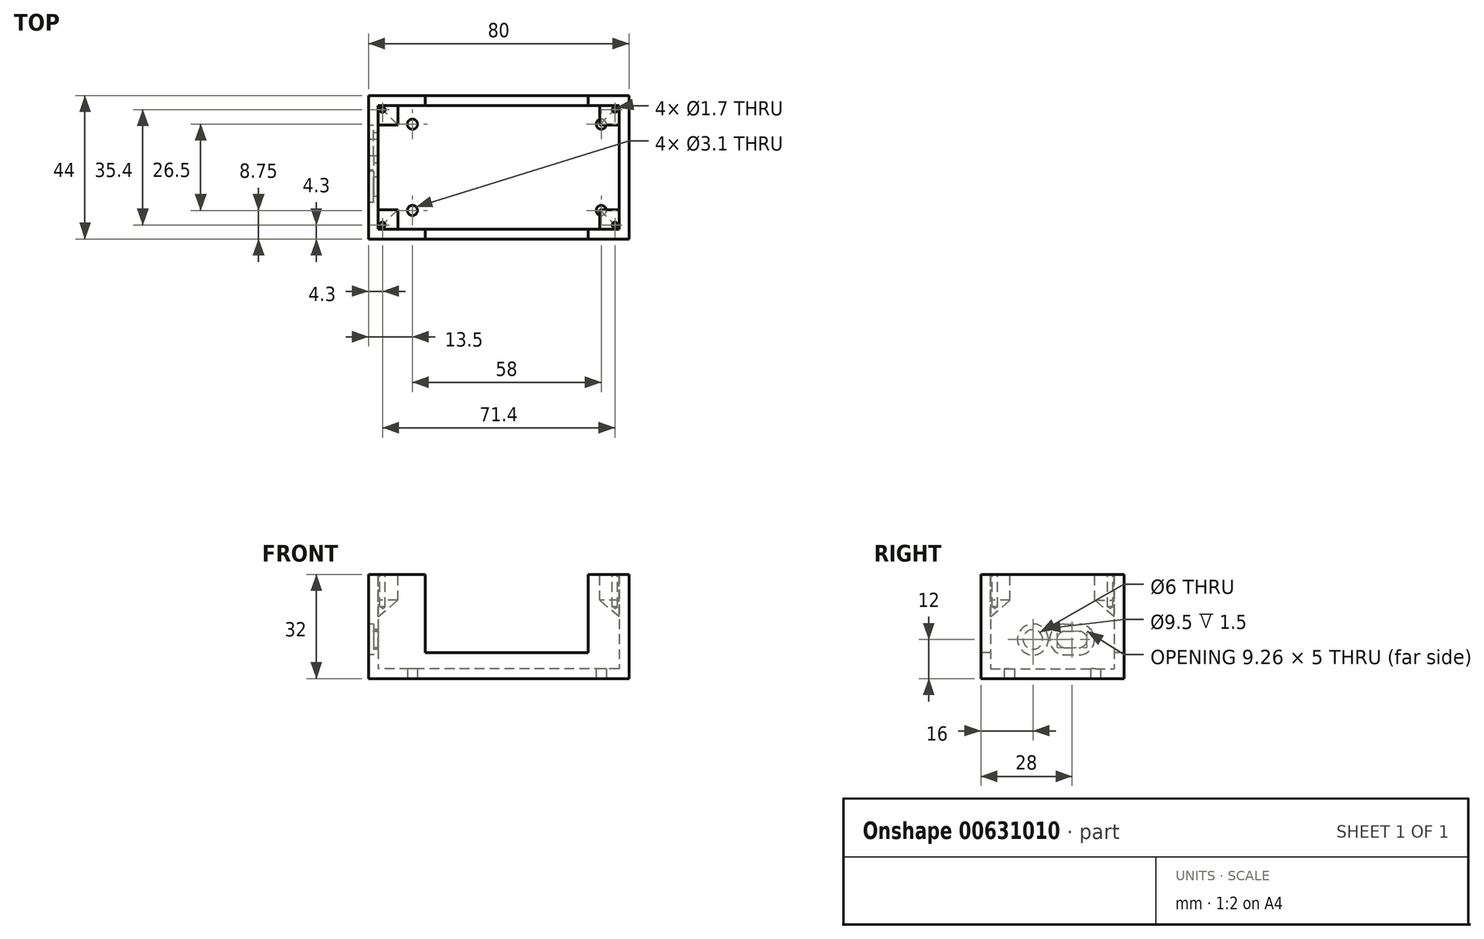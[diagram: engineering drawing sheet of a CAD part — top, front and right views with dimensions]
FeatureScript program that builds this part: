
annotation { "Feature Type Name" : "Feature", "Feature Type Description" : "" }
export const myFeature = defineFeature(function(context is Context, id is Id, definition is map)
    precondition{}
    {
        {
            var Q0;
            Q0=qCreatedBy(makeId("Top.planeOp"),FACE);
            var sketch = newSketch(context, id + "F0", { "sketchPlane" : qUnion([Q0])});
            skLineSegment(sketch, "E0.bottom", {"start": v(40, -22) * mm, "end": v(-40, -22) * mm});
            skLineSegment(sketch, "E0.top", {"start": v(40, 22) * mm, "end": v(-40, 22) * mm});
            skLineSegment(sketch, "E0.left", {"start": v(40, -22) * mm, "end": v(40, 22) * mm});
            skLineSegment(sketch, "E0.right", {"start": v(-40, -22) * mm, "end": v(-40, 22) * mm});
            skPoint(sketch, "E0.middle", {"position": v(0, 0) * mm});
            skSolve(sketch);
        }
        {
            var Q0;
            Q0=makeQuery(id+"F0.imprint","IMPRINT",FACE,{"disambiguationData":[TD([[makeQuery(id+"F0.imprint","IMPRINT",EDGE,{"derivedFrom":sQuery(id+"F0.wireOp",EDGE,"E0.bottom")}),-1.0]])]});
            extrude(context, id + "F1", {"entities" : qUnion([Q0]), "depth" : 32 * mm, "offsetDistance" : 25 * mm});
        }
        {
            var Q0;
            Q0=makeQuery(id+"F1.opExtrude","CAP_FACE",FACE,{"disambiguationData":[OSD([sQuery(id+"F0.wireOp",EDGE,"E0.bottom"),sQuery(id+"F0.wireOp",EDGE,"E0.top"),sQuery(id+"F0.wireOp",EDGE,"E0.left"),sQuery(id+"F0.wireOp",EDGE,"E0.right")])],"isStart":false});
            shell(context, id + "F2", {"entities" : qUnion([Q0]), "thickness" : 3 * mm});
        }
        {
            var Q0;
            Q0=makeQuery(id+"F1.opExtrude","SWEPT_FACE",FACE,{"disambiguationData":[OSD([sQuery(id+"F0.wireOp",EDGE,"E0.right")])]});
            var sketch = newSketch(context, id + "F3", { "sketchPlane" : qUnion([Q0])});
            skPoint(sketch, "E1", {"position": v(6, 12) * mm});
            skSolve(sketch);
        }
        {
            var Q0;
            {var subQ0=sQuery(id+"F0.wireOp",EDGE,"E0.right");Q0=makeQuery(id+"F3.imprint","IMPRINT",FACE,{"disambiguationData":[TD([[makeQuery(id+"F3.imprint","IMPRINT",EDGE,{"derivedFrom":makeQuery(id+"F1.opExtrude","CAP_EDGE",EDGE,{"disambiguationData":[OSD([subQ0])],"isStart":true})}),-1.0]])]});}
            var sketch = newSketch(context, id + "F4", { "sketchPlane" : qUnion([Q0])});
            skPoint(sketch, "E2", {"position": v(-6, 12) * mm});
            skPoint(sketch, "E3", {"position": v(-8.13, 12) * mm});
            skPoint(sketch, "E4", {"position": v(-3.87, 12) * mm});
            skSolve(sketch);
        }
        {
            var Q0;
            Q0=sQuery(id+"F3.wireOp",VERTEX,"E1");
            var Q1;
            Q1=makeQuery(id+"F1.opExtrude","SWEPT_BODY",BODY,{"disambiguationData":[OSD([sQuery(id+"F0.wireOp",EDGE,"E0.bottom"),sQuery(id+"F0.wireOp",EDGE,"E0.top"),sQuery(id+"F0.wireOp",EDGE,"E0.left"),sQuery(id+"F0.wireOp",EDGE,"E0.right")])]});
            hole(context, id + "F5", {"style" : HoleStyle.C_BORE, "endStyle" : HoleEndStyle.BLIND, "holeDiameter" : 6 * mm, "cBoreDiameter" : 9.5 * mm, "cBoreDepth" : 1.5 * mm, "majorDiameter" : 5 * mm, "holeDepth" : 10 * mm, "isTappedThrough" : true, "tappedDepth" : 12 * mm, "tapClearance" : 3, "locations" : qUnion([Q0]), "scope" : qUnion([Q1])});
        }
        {
            var Q0;
            Q0=sQuery(id+"F4.wireOp",VERTEX,"E3");
            var Q1;
            Q1=sQuery(id+"F4.wireOp",VERTEX,"E4");
            var Q2;
            Q2=makeQuery(id+"F1.opExtrude","SWEPT_BODY",BODY,{"disambiguationData":[OSD([sQuery(id+"F0.wireOp",EDGE,"E0.bottom"),sQuery(id+"F0.wireOp",EDGE,"E0.top"),sQuery(id+"F0.wireOp",EDGE,"E0.left"),sQuery(id+"F0.wireOp",EDGE,"E0.right")])]});
            hole(context, id + "F6", {"style" : HoleStyle.C_BORE, "endStyle" : HoleEndStyle.BLIND, "holeDiameter" : 5 * mm, "cBoreDiameter" : 9.5 * mm, "cBoreDepth" : 1.5 * mm, "majorDiameter" : 5 * mm, "holeDepth" : 10 * mm, "isTappedThrough" : true, "tappedDepth" : 12 * mm, "tapClearance" : 3, "locations" : qUnion([Q0, Q1]), "scope" : qUnion([Q2])});
        }
        {
            var Q0;
            Q0=makeQuery(id+"F1.opExtrude","SWEPT_FACE",FACE,{"disambiguationData":[OSD([sQuery(id+"F0.wireOp",EDGE,"E0.right")])]});
            var sketch = newSketch(context, id + "F7", { "sketchPlane" : qUnion([Q0])});
            skLineSegment(sketch, "E5.bottom", {"start": v(-3.5, 9.5) * mm, "end": v(-8.5, 9.5) * mm});
            skLineSegment(sketch, "E5.top", {"start": v(-3.5, 14.5) * mm, "end": v(-8.5, 14.5) * mm});
            skLineSegment(sketch, "E5.left", {"start": v(-3.5, 9.5) * mm, "end": v(-3.5, 14.5) * mm});
            skLineSegment(sketch, "E5.right", {"start": v(-8.5, 9.5) * mm, "end": v(-8.5, 14.5) * mm});
            skPoint(sketch, "E5.middle", {"position": v(-6, 12) * mm});
            skSolve(sketch);
        }
        {
            var Q0;
            {var subQ0=sQuery(id+"F7.wireOp",EDGE,"E5.top");var subQ1=makeQuery(id+"F6.hole-1.boolean.opBoolean","COPY",EDGE,{"derivedFrom":makeQuery(id+"F6.hole-1.opRevolve","SWEPT_EDGE",EDGE,{"disambiguationData":[OSD([sQuery(id+"F6.hole-1.sketch.wireOp",EDGE,"core_line_2"),sQuery(id+"F6.hole-1.sketch.wireOp",EDGE,"core_line_3")])]})});var subQ2=makeQuery(id+"F7.imprint","INTERSECT",VERTEX,{"derivedFrom":[subQ1,subQ0]});Q0=makeQuery(id+"F7.imprint","IMPRINT",FACE,{"disambiguationData":[TD([[makeQuery(id+"F7.imprint","IMPRINT",EDGE,{"disambiguationData":[TD([[subQ2,-1.0]])],"derivedFrom":subQ0}),1.0]])]});}
            var Q1;
            {var subQ0=sQuery(id+"F7.wireOp",EDGE,"E5.bottom");var subQ1=makeQuery(id+"F6.hole-1.boolean.opBoolean","COPY",EDGE,{"derivedFrom":makeQuery(id+"F6.hole-1.opRevolve","SWEPT_EDGE",EDGE,{"disambiguationData":[OSD([sQuery(id+"F6.hole-1.sketch.wireOp",EDGE,"core_line_2"),sQuery(id+"F6.hole-1.sketch.wireOp",EDGE,"core_line_3")])]})});var subQ2=makeQuery(id+"F7.imprint","INTERSECT",VERTEX,{"derivedFrom":[subQ1,subQ0]});Q1=makeQuery(id+"F7.imprint","IMPRINT",FACE,{"disambiguationData":[TD([[makeQuery(id+"F7.imprint","IMPRINT",EDGE,{"disambiguationData":[TD([[subQ2,-1.0]])],"derivedFrom":subQ0}),-1.0]])]});}
            extrude(context, id + "F8", {"entities" : qUnion([Q0, Q1]), "operationType" : NewBodyOperationType.REMOVE, "oppositeDirection" : true, "depth" : 10 * mm, "offsetDistance" : 25 * mm});
        }
        {
            var Q0;
            Q0=makeQuery(id+"F1.opExtrude","CAP_FACE",FACE,{"disambiguationData":[OSD([sQuery(id+"F0.wireOp",EDGE,"E0.bottom"),sQuery(id+"F0.wireOp",EDGE,"E0.top"),sQuery(id+"F0.wireOp",EDGE,"E0.left"),sQuery(id+"F0.wireOp",EDGE,"E0.right")])],"isStart":true});
            var sketch = newSketch(context, id + "F9", { "sketchPlane" : qUnion([Q0])});
            skPoint(sketch, "E6", {"position": v(-26.5, 13.25) * mm});
            skPoint(sketch, "E7", {"position": v(31.5, 13.25) * mm});
            skPoint(sketch, "E8", {"position": v(31.5, -13.25) * mm});
            skPoint(sketch, "E9", {"position": v(-26.5, -13.25) * mm});
            skSolve(sketch);
        }
        {
            var Q0;
            Q0=sQuery(id+"F9.wireOp",VERTEX,"E9");
            var Q1;
            Q1=sQuery(id+"F9.wireOp",VERTEX,"E6");
            var Q2;
            Q2=sQuery(id+"F9.wireOp",VERTEX,"E7");
            var Q3;
            Q3=sQuery(id+"F9.wireOp",VERTEX,"E8");
            var Q4;
            Q4=makeQuery(id+"F1.opExtrude","SWEPT_BODY",BODY,{"disambiguationData":[OSD([sQuery(id+"F0.wireOp",EDGE,"E0.bottom"),sQuery(id+"F0.wireOp",EDGE,"E0.top"),sQuery(id+"F0.wireOp",EDGE,"E0.left"),sQuery(id+"F0.wireOp",EDGE,"E0.right")])]});
            hole(context, id + "F10", {"style" : HoleStyle.SIMPLE, "endStyle" : HoleEndStyle.BLIND, "holeDiameter" : 3.1 * mm, "majorDiameter" : 5 * mm, "holeDepth" : 10 * mm, "isTappedThrough" : true, "tappedDepth" : 12 * mm, "tapClearance" : 3, "locations" : qUnion([Q0, Q1, Q2, Q3]), "scope" : qUnion([Q4])});
        }
        {
            var Q0;
            Q0=makeQuery(id+"F1.opExtrude","SWEPT_FACE",FACE,{"disambiguationData":[OSD([sQuery(id+"F0.wireOp",EDGE,"E0.right")])]});
            var sketch = newSketch(context, id + "F11", { "sketchPlane" : qUnion([Q0])});
            skLineSegment(sketch, "E10.bottom", {"start": v(-3.5, 7.25) * mm, "end": v(-8.5, 7.25) * mm});
            skLineSegment(sketch, "E10.top", {"start": v(-3.5, 16.75) * mm, "end": v(-8.5, 16.75) * mm});
            skLineSegment(sketch, "E10.left", {"start": v(-3.5, 7.25) * mm, "end": v(-3.5, 16.75) * mm});
            skLineSegment(sketch, "E10.right", {"start": v(-8.5, 7.25) * mm, "end": v(-8.5, 16.75) * mm});
            skPoint(sketch, "E10.middle", {"position": v(-6, 12) * mm});
            skSolve(sketch);
        }
        {
            var Q0;
            {var subQ0=sQuery(id+"F11.wireOp",EDGE,"E10.top");var subQ1=makeQuery(id+"F6.hole-1.boolean.opBoolean","COPY",EDGE,{"derivedFrom":makeQuery(id+"F6.hole-1.opRevolve","SWEPT_EDGE",EDGE,{"disambiguationData":[OSD([sQuery(id+"F6.hole-1.sketch.wireOp",EDGE,"cbore_start_line_2"),sQuery(id+"F6.hole-1.sketch.wireOp",EDGE,"cbore_start_line_3")])]})});var subQ2=makeQuery(id+"F11.imprint","INTERSECT",VERTEX,{"derivedFrom":[subQ1,subQ0]});Q0=makeQuery(id+"F11.imprint","IMPRINT",FACE,{"disambiguationData":[TD([[makeQuery(id+"F11.imprint","IMPRINT",EDGE,{"disambiguationData":[TD([[subQ2,-1.0]])],"derivedFrom":subQ0}),1.0]])]});}
            var Q1;
            {var subQ0=sQuery(id+"F11.wireOp",EDGE,"E10.bottom");var subQ1=makeQuery(id+"F6.hole-1.boolean.opBoolean","COPY",EDGE,{"derivedFrom":makeQuery(id+"F6.hole-1.opRevolve","SWEPT_EDGE",EDGE,{"disambiguationData":[OSD([sQuery(id+"F6.hole-1.sketch.wireOp",EDGE,"cbore_start_line_2"),sQuery(id+"F6.hole-1.sketch.wireOp",EDGE,"cbore_start_line_3")])]})});var subQ2=makeQuery(id+"F11.imprint","INTERSECT",VERTEX,{"derivedFrom":[subQ1,subQ0]});Q1=makeQuery(id+"F11.imprint","IMPRINT",FACE,{"disambiguationData":[TD([[makeQuery(id+"F11.imprint","IMPRINT",EDGE,{"disambiguationData":[TD([[subQ2,-1.0]])],"derivedFrom":subQ0}),-1.0]])]});}
            extrude(context, id + "F12", {"entities" : qUnion([Q0, Q1]), "operationType" : NewBodyOperationType.REMOVE, "oppositeDirection" : true, "depth" : 1.5 * mm, "offsetDistance" : 25 * mm});
        }
        {
            var Q0;
            Q0=makeQuery(id+"F1.opExtrude","SWEPT_FACE",FACE,{"disambiguationData":[OSD([sQuery(id+"F0.wireOp",EDGE,"E0.bottom")])]});
            var sketch = newSketch(context, id + "F13", { "sketchPlane" : qUnion([Q0])});
            skLineSegment(sketch, "E11.bottom", {"start": v(-22.5, 32) * mm, "end": v(27.5, 32) * mm});
            skLineSegment(sketch, "E11.top", {"start": v(-22.5, 8) * mm, "end": v(27.5, 8) * mm});
            skLineSegment(sketch, "E11.left", {"start": v(-22.5, 32) * mm, "end": v(-22.5, 8) * mm});
            skLineSegment(sketch, "E11.right", {"start": v(27.5, 32) * mm, "end": v(27.5, 8) * mm});
            skSolve(sketch);
        }
        {
            var Q0;
            Q0=makeQuery(id+"F13.imprint","IMPRINT",FACE,{"disambiguationData":[TD([[makeQuery(id+"F13.imprint","IMPRINT",EDGE,{"derivedFrom":sQuery(id+"F13.wireOp",EDGE,"E11.bottom")}),1.0]])]});
            extrude(context, id + "F14", {"entities" : qUnion([Q0]), "operationType" : NewBodyOperationType.REMOVE, "oppositeDirection" : true, "depth" : 60 * mm, "offsetDistance" : 25 * mm});
        }
        {
            var Q0;
            {var subQ0=sQuery(id+"F0.wireOp",EDGE,"E0.bottom");var subQ1=sQuery(id+"F0.wireOp",EDGE,"E0.left");var subQ2=sQuery(id+"F0.wireOp",EDGE,"E0.top");Q0=makeQuery(id+"F14.boolean.opBoolean","SPLIT",FACE,{"disambiguationData":[TD([makeQuery(id+"F1.opExtrude","SWEPT_FACE",FACE,{"disambiguationData":[OSD([subQ1])]})])],"derivedFrom":makeQuery(id+"F1.opExtrude","CAP_FACE",FACE,{"disambiguationData":[OSD([subQ0,subQ2,subQ1,sQuery(id+"F0.wireOp",EDGE,"E0.right")])],"isStart":false})});}
            var sketch = newSketch(context, id + "F15", { "sketchPlane" : qUnion([Q0])});
            skLineSegment(sketch, "E12.bottom", {"start": v(-37, 19) * mm, "end": v(-31, 19) * mm});
            skLineSegment(sketch, "E12.top", {"start": v(-37, 13) * mm, "end": v(-31, 13) * mm});
            skLineSegment(sketch, "E12.left", {"start": v(-37, 19) * mm, "end": v(-37, 13) * mm});
            skLineSegment(sketch, "E12.right", {"start": v(-31, 19) * mm, "end": v(-31, 13) * mm});
            skLineSegment(sketch, "E13.bottom", {"start": v(-37, -19) * mm, "end": v(-31, -19) * mm});
            skLineSegment(sketch, "E13.top", {"start": v(-37, -13) * mm, "end": v(-31, -13) * mm});
            skLineSegment(sketch, "E13.left", {"start": v(-37, -19) * mm, "end": v(-37, -13) * mm});
            skLineSegment(sketch, "E13.right", {"start": v(-31, -19) * mm, "end": v(-31, -13) * mm});
            skLineSegment(sketch, "E14.bottom", {"start": v(37, 19) * mm, "end": v(31, 19) * mm});
            skLineSegment(sketch, "E14.top", {"start": v(37, 13) * mm, "end": v(31, 13) * mm});
            skLineSegment(sketch, "E14.left", {"start": v(37, 19) * mm, "end": v(37, 13) * mm});
            skLineSegment(sketch, "E14.right", {"start": v(31, 19) * mm, "end": v(31, 13) * mm});
            skLineSegment(sketch, "E15.bottom", {"start": v(37, -19) * mm, "end": v(31, -19) * mm});
            skLineSegment(sketch, "E15.top", {"start": v(37, -13) * mm, "end": v(31, -13) * mm});
            skLineSegment(sketch, "E15.left", {"start": v(37, -19) * mm, "end": v(37, -13) * mm});
            skLineSegment(sketch, "E15.right", {"start": v(31, -19) * mm, "end": v(31, -13) * mm});
            skSolve(sketch);
        }
        {
            var Q0;
            Q0=makeQuery(id+"F15.imprint","IMPRINT",FACE,{"disambiguationData":[TD([[makeQuery(id+"F15.imprint","IMPRINT",EDGE,{"derivedFrom":sQuery(id+"F15.wireOp",EDGE,"E12.bottom")}),-1.0]])]});
            var Q1;
            Q1=makeQuery(id+"F15.imprint","IMPRINT",FACE,{"disambiguationData":[TD([[makeQuery(id+"F15.imprint","IMPRINT",EDGE,{"derivedFrom":sQuery(id+"F15.wireOp",EDGE,"E13.bottom")}),1.0]])]});
            var Q2;
            Q2=makeQuery(id+"F15.imprint","IMPRINT",FACE,{"disambiguationData":[TD([[makeQuery(id+"F15.imprint","IMPRINT",EDGE,{"derivedFrom":sQuery(id+"F15.wireOp",EDGE,"E15.bottom")}),-1.0]])]});
            var Q3;
            Q3=makeQuery(id+"F15.imprint","IMPRINT",FACE,{"disambiguationData":[TD([[makeQuery(id+"F15.imprint","IMPRINT",EDGE,{"derivedFrom":sQuery(id+"F15.wireOp",EDGE,"E14.bottom")}),1.0]])]});
            extrude(context, id + "F16", {"entities" : qUnion([Q0, Q1, Q2, Q3]), "oppositeDirection" : true, "depth" : 13 * mm, "offsetDistance" : 25 * mm});
        }
        {
            var Q0;
            Q0=makeQuery(id+"F16.opExtrude","CAP_EDGE",EDGE,{"disambiguationData":[OSD([sQuery(id+"F15.wireOp",EDGE,"E12.top")])],"isStart":false});
            var Q1;
            Q1=makeQuery(id+"F16.opExtrude","CAP_EDGE",EDGE,{"disambiguationData":[OSD([sQuery(id+"F15.wireOp",EDGE,"E12.right")])],"isStart":false});
            var Q2;
            Q2=makeQuery(id+"F16.opExtrude","CAP_EDGE",EDGE,{"disambiguationData":[OSD([sQuery(id+"F15.wireOp",EDGE,"E14.right")])],"isStart":false});
            var Q3;
            Q3=makeQuery(id+"F16.opExtrude","CAP_EDGE",EDGE,{"disambiguationData":[OSD([sQuery(id+"F15.wireOp",EDGE,"E14.top")])],"isStart":false});
            var Q4;
            Q4=makeQuery(id+"F16.opExtrude","CAP_EDGE",EDGE,{"disambiguationData":[OSD([sQuery(id+"F15.wireOp",EDGE,"E15.top")])],"isStart":false});
            var Q5;
            Q5=makeQuery(id+"F16.opExtrude","CAP_EDGE",EDGE,{"disambiguationData":[OSD([sQuery(id+"F15.wireOp",EDGE,"E15.right")])],"isStart":false});
            var Q6;
            Q6=makeQuery(id+"F16.opExtrude","CAP_EDGE",EDGE,{"disambiguationData":[OSD([sQuery(id+"F15.wireOp",EDGE,"E13.right")])],"isStart":false});
            var Q7;
            Q7=makeQuery(id+"F16.opExtrude","CAP_EDGE",EDGE,{"disambiguationData":[OSD([sQuery(id+"F15.wireOp",EDGE,"E13.top")])],"isStart":false});
            chamfer(context, id + "F17", {"entities" : qUnion([Q0, Q1, Q2, Q3, Q4, Q5, Q6, Q7]), "chamferType" : ChamferType.OFFSET_ANGLE, "width" : 6 * mm, "oppositeDirection" : true, "angle" : 40 * degree});
        }
        {
            var Q0;
            Q0=makeQuery(id+"F16.opExtrude","CAP_FACE",FACE,{"disambiguationData":[OSD([sQuery(id+"F15.wireOp",EDGE,"E14.bottom"),sQuery(id+"F15.wireOp",EDGE,"E14.top"),sQuery(id+"F15.wireOp",EDGE,"E14.left"),sQuery(id+"F15.wireOp",EDGE,"E14.right")])],"isStart":true});
            var sketch = newSketch(context, id + "F18", { "sketchPlane" : qUnion([Q0])});
            skPoint(sketch, "E16", {"position": v(35.7, 17.7) * mm});
            skPoint(sketch, "E17", {"position": v(-35.7, 17.7) * mm});
            skPoint(sketch, "E18", {"position": v(-35.7, -17.7) * mm});
            skPoint(sketch, "E19", {"position": v(35.7, -17.7) * mm});
            skSolve(sketch);
        }
        {
            var Q0;
            Q0=sQuery(id+"F18.wireOp",VERTEX,"E17");
            var Q1;
            Q1=sQuery(id+"F18.wireOp",VERTEX,"E19");
            var Q2;
            Q2=sQuery(id+"F18.wireOp",VERTEX,"E18");
            var Q3;
            Q3=sQuery(id+"F18.wireOp",VERTEX,"E16");
            var Q4;
            Q4=makeQuery(id+"F16.opExtrude","SWEPT_BODY",BODY,{"disambiguationData":[OSD([sQuery(id+"F15.wireOp",EDGE,"E14.bottom"),sQuery(id+"F15.wireOp",EDGE,"E14.top"),sQuery(id+"F15.wireOp",EDGE,"E14.left"),sQuery(id+"F15.wireOp",EDGE,"E14.right")])]});
            var Q5;
            Q5=makeQuery(id+"F16.opExtrude","SWEPT_BODY",BODY,{"disambiguationData":[OSD([sQuery(id+"F15.wireOp",EDGE,"E12.bottom"),sQuery(id+"F15.wireOp",EDGE,"E12.top"),sQuery(id+"F15.wireOp",EDGE,"E12.left"),sQuery(id+"F15.wireOp",EDGE,"E12.right")])]});
            var Q6;
            Q6=makeQuery(id+"F16.opExtrude","SWEPT_BODY",BODY,{"disambiguationData":[OSD([sQuery(id+"F15.wireOp",EDGE,"E15.bottom"),sQuery(id+"F15.wireOp",EDGE,"E15.top"),sQuery(id+"F15.wireOp",EDGE,"E15.left"),sQuery(id+"F15.wireOp",EDGE,"E15.right")])]});
            var Q7;
            Q7=makeQuery(id+"F16.opExtrude","SWEPT_BODY",BODY,{"disambiguationData":[OSD([sQuery(id+"F15.wireOp",EDGE,"E13.bottom"),sQuery(id+"F15.wireOp",EDGE,"E13.top"),sQuery(id+"F15.wireOp",EDGE,"E13.left"),sQuery(id+"F15.wireOp",EDGE,"E13.right")])]});
            hole(context, id + "F19", {"style" : HoleStyle.SIMPLE, "endStyle" : HoleEndStyle.BLIND, "holeDiameter" : 1.7 * mm, "majorDiameter" : 5 * mm, "holeDepth" : 10 * mm, "isTappedThrough" : true, "tappedDepth" : 12 * mm, "tapClearance" : 3, "locations" : qUnion([Q0, Q1, Q2, Q3]), "scope" : qUnion([Q4, Q5, Q6, Q7])});
        }
    });
